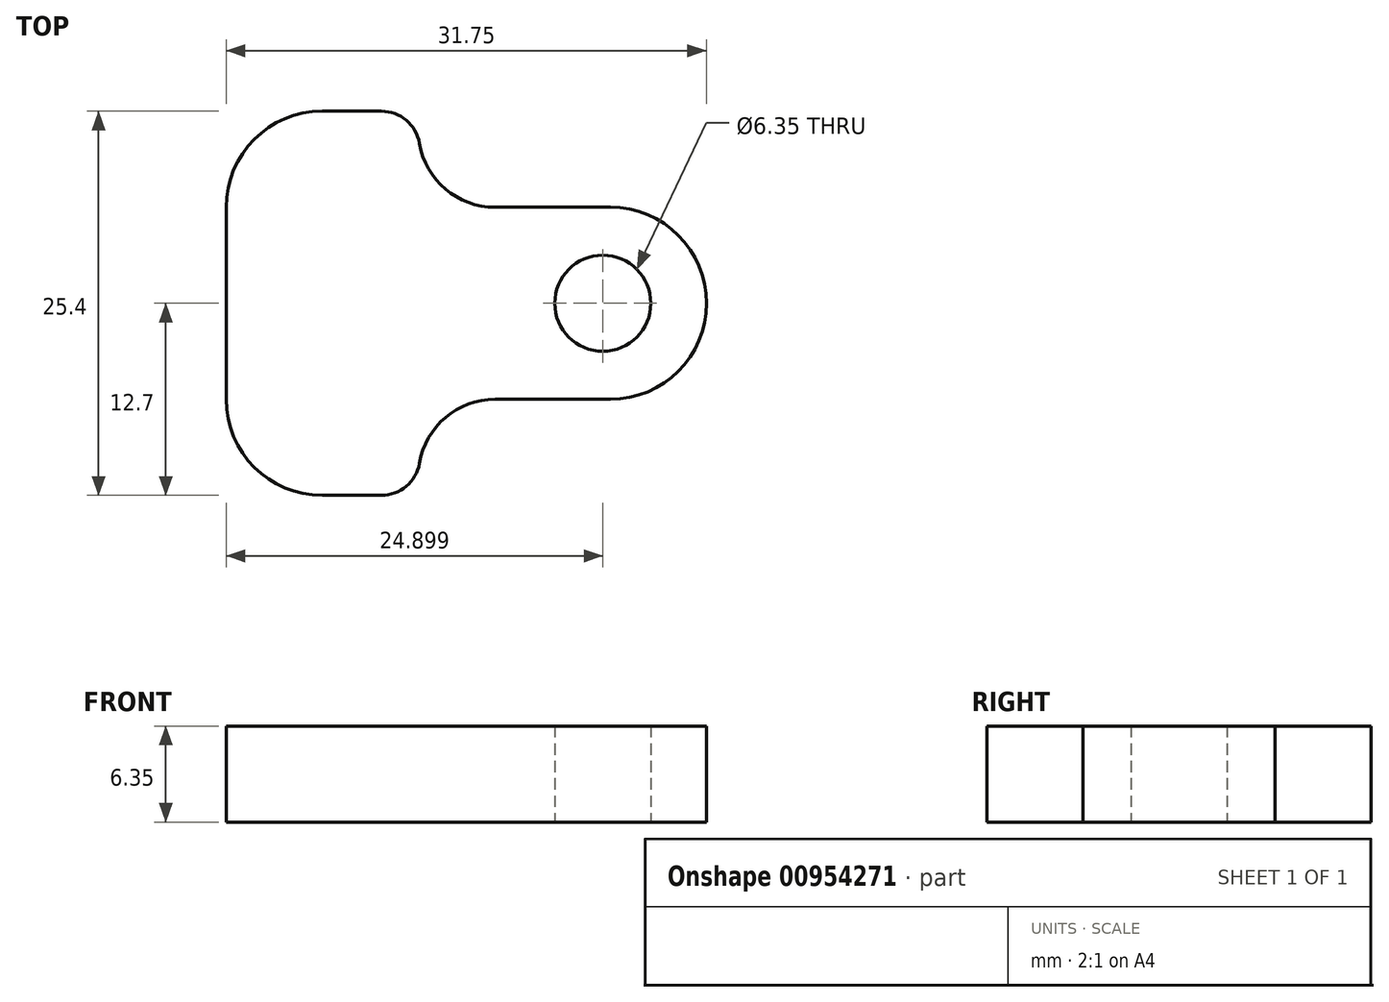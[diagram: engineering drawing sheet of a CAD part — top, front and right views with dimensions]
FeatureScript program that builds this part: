
annotation { "Feature Type Name" : "Feature", "Feature Type Description" : "" }
export const myFeature = defineFeature(function(context is Context, id is Id, definition is map)
    precondition{}
    {
        {
            var Q0;
            Q0=qCreatedBy(makeId("Top.planeOp"),FACE);
            var sketch = newSketch(context, id + "F0", { "sketchPlane" : qUnion([Q0])});
            skLineSegment(sketch, "E0.bottom", {"start": v(6.35, 12.7) * mm, "end": v(0, 12.7) * mm});
            skLineSegment(sketch, "E0.top", {"start": v(6.35, -12.7) * mm, "end": v(0, -12.7) * mm});
            skLineSegment(sketch, "E0.right", {"start": v(-6.35, 6.35) * mm, "end": v(-6.35, -6.35) * mm});
            skPoint(sketch, "E0.middle", {"position": v(0, 0) * mm});
            skPoint(sketch, "E1.visualSharp", {"position": v(-6.35, 12.7) * mm});
            skArc(sketch, "E1.filletArc", {"start": v(0, 12.7) * mm, "mid": v(-4.5, 10.84) * mm, "end": v(-6.35, 6.35) * mm});
            skPoint(sketch, "E2.visualSharp", {"position": v(-6.35, -12.7) * mm});
            skArc(sketch, "E2.filletArc", {"start": v(-6.35, -6.35) * mm, "mid": v(-4.5, -10.84) * mm, "end": v(0, -12.7) * mm});
            skLineSegment(sketch, "E3.bottom", {"start": v(6.35, 6.35) * mm, "end": v(19.05, 6.35) * mm});
            skLineSegment(sketch, "E3.top", {"start": v(12.7, -6.35) * mm, "end": v(19.05, -6.35) * mm});
            skLineSegment(sketch, "E3.right", {"start": v(25.4, 0) * mm, "end": v(25.4, 0) * mm});
            skPoint(sketch, "E4.visualSharp", {"position": v(6.35, -6.35) * mm});
            skCircle(sketch, "E5", {"center": v(18.55, 0) * mm, "radius": 3.18 * mm});
            skPoint(sketch, "E6.visualSharp", {"position": v(25.4, 6.35) * mm});
            skArc(sketch, "E6.filletArc", {"start": v(25.4, 0) * mm, "mid": v(23.54, 4.5) * mm, "end": v(19.05, 6.35) * mm});
            skPoint(sketch, "E7.visualSharp", {"position": v(25.4, -6.35) * mm});
            skArc(sketch, "E7.filletArc", {"start": v(19.05, -6.35) * mm, "mid": v(23.54, -4.5) * mm, "end": v(25.4, 0) * mm});
            skLineSegment(sketch, "E8", {"start": v(12.7, -6.35) * mm, "end": v(6.35, -6.35) * mm});
            skLineSegment(sketch, "E9", {"start": v(6.35, 6.35) * mm, "end": v(6.35, 12.7) * mm});
            skLineSegment(sketch, "E10", {"start": v(6.35, -12.7) * mm, "end": v(6.35, -6.35) * mm});
            skSolve(sketch);
        }
        {
            var Q0;
            Q0=makeQuery(id+"F0.imprint","IMPRINT",FACE,{"disambiguationData":[TD([[makeQuery(id+"F0.imprint","IMPRINT",EDGE,{"derivedFrom":sQuery(id+"F0.wireOp",EDGE,"E0.bottom")}),1.0]])]});
            extrude(context, id + "F1", {"entities" : qUnion([Q0]), "depth" : 6.35 * mm, "offsetDistance" : 25.4 * mm});
        }
        {
            var Q0;
            Q0=makeQuery(id+"F1.opExtrude","SWEPT_EDGE",EDGE,{"disambiguationData":[OSD([sQuery(id+"F0.wireOp",EDGE,"E8"),sQuery(id+"F0.wireOp",EDGE,"E10")])]});
            var Q1;
            Q1=makeQuery(id+"F1.opExtrude","SWEPT_EDGE",EDGE,{"disambiguationData":[OSD([sQuery(id+"F0.wireOp",EDGE,"E3.bottom"),sQuery(id+"F0.wireOp",EDGE,"E9")])]});
            fillet(context, id + "F2", {"entities" : qUnion([Q0, Q1]), "radius" : 5.08 * mm, "tangentPropagation" : true, "allowEdgeOverflow" : false});
        }
        {
            var Q0;
            Q0=makeQuery(id+"F1.opExtrude","SWEPT_EDGE",EDGE,{"disambiguationData":[OSD([sQuery(id+"F0.wireOp",EDGE,"E0.bottom"),sQuery(id+"F0.wireOp",EDGE,"E9")])]});
            var Q1;
            Q1=makeQuery(id+"F1.opExtrude","SWEPT_EDGE",EDGE,{"disambiguationData":[OSD([sQuery(id+"F0.wireOp",EDGE,"E0.top"),sQuery(id+"F0.wireOp",EDGE,"E10")])]});
            fillet(context, id + "F3", {"entities" : qUnion([Q0, Q1]), "radius" : 2.54 * mm, "tangentPropagation" : true, "allowEdgeOverflow" : false});
        }
    });
